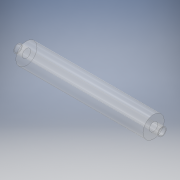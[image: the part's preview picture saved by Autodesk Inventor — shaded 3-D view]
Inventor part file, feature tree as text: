
AUTODESK INVENTOR PART (.ipt)
format: ipt  version: 2017 SP1 (Build 210196100, 196)  size: 136,704 bytes
history: native  units: mm
features: extrude x6, sketch x6
ambient origin geometry x8: Origin, YZ Plane, XZ Plane, XY Plane, X Axis, Y Axis, Z Axis, Center Point
bodies: Solid1 (feature_tree)
feature tree (12):
  extrude  "Extrusion1"  Depth=170.0mm TaperAngle=0.0deg
  extrude  "Extrusion2"  Depth=10.0mm TaperAngle=0.0deg
  extrude  "Extrusion3"  Depth=10.0mm TaperAngle=0.0deg
  extrude  "Extrusion4"  Depth=10.0mm TaperAngle=0.0deg
  extrude  "Extrusion5"  Depth=10.0mm
  extrude  "Extrusion6"  [1 undecoded]
  sketch  "Sketch1"  dims[d0=25.0mm d1=170.0mm d2=0.0mm]
  sketch  "Sketch2"  dims[d3=25.0mm d4=10.0mm d5=0.0mm]
  sketch  "Sketch3"  dims[d6=10.0mm d7=10.0mm d8=0.0mm]
  sketch  "Sketch4"  dims[d9=25.0mm d10=10.0mm d11=0.0mm]
  sketch  "Sketch5"  dims[d12=10.0mm d13=0.0mm d14=8.0mm]
  sketch  "Sketch6"  dims[d15=170.0mm d16=0.0mm]
note: 1 required parameter value undecoded (feature->parameter linkage not recoverable at this tier; creation-order binding heuristic only, values carry confidence <= 0.55)
